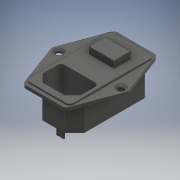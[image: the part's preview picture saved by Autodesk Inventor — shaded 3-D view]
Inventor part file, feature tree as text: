
AUTODESK INVENTOR PART (.ipt)
format: ipt  version: 2017 (Build 210142000, 142)  size: 274,432 bytes
history: native  units: mm
features: sketch x8, extrude x7, chamfer x1, hole x1, fillet x1
ambient origin geometry x8: Origin, YZ Plane, XZ Plane, XY Plane, X Axis, Y Axis, Z Axis, Center Point
bodies: Solide1 (feature_tree)
feature tree (18):
  extrude  "Extrusion1"  Depth=26.8mm
  chamfer  "Chanfrein1"  Distance=47.0mm
  extrude  "Extrusion2"  Depth=18.0mm TaperAngle=0.0deg
  extrude  "Extrusion3"  Depth=6.5mm TaperAngle=45.0deg
  extrude  "Extrusion4"  Depth=58.8mm
  extrude  "Extrusion5"  Depth=29.4mm
  extrude  "Extrusion6"  Depth=48.8mm
  extrude  "Extrusion7"  Depth=24.4mm
  hole  "Perçage1"  [1 undecoded]
  fillet  "Congé1"  Radius=27.0mm
  sketch  "Esquisse1"
  sketch  "Esquisse2"
  sketch  "Esquisse3"
  sketch  "Esquisse4"
  sketch  "Esquisse5"
  sketch  "Esquisse6"
  sketch  "Esquisse7"
  sketch  "Esquisse8"
note: 1 required parameter value undecoded (feature->parameter linkage not recoverable at this tier; creation-order binding heuristic only, values carry confidence <= 0.55)
